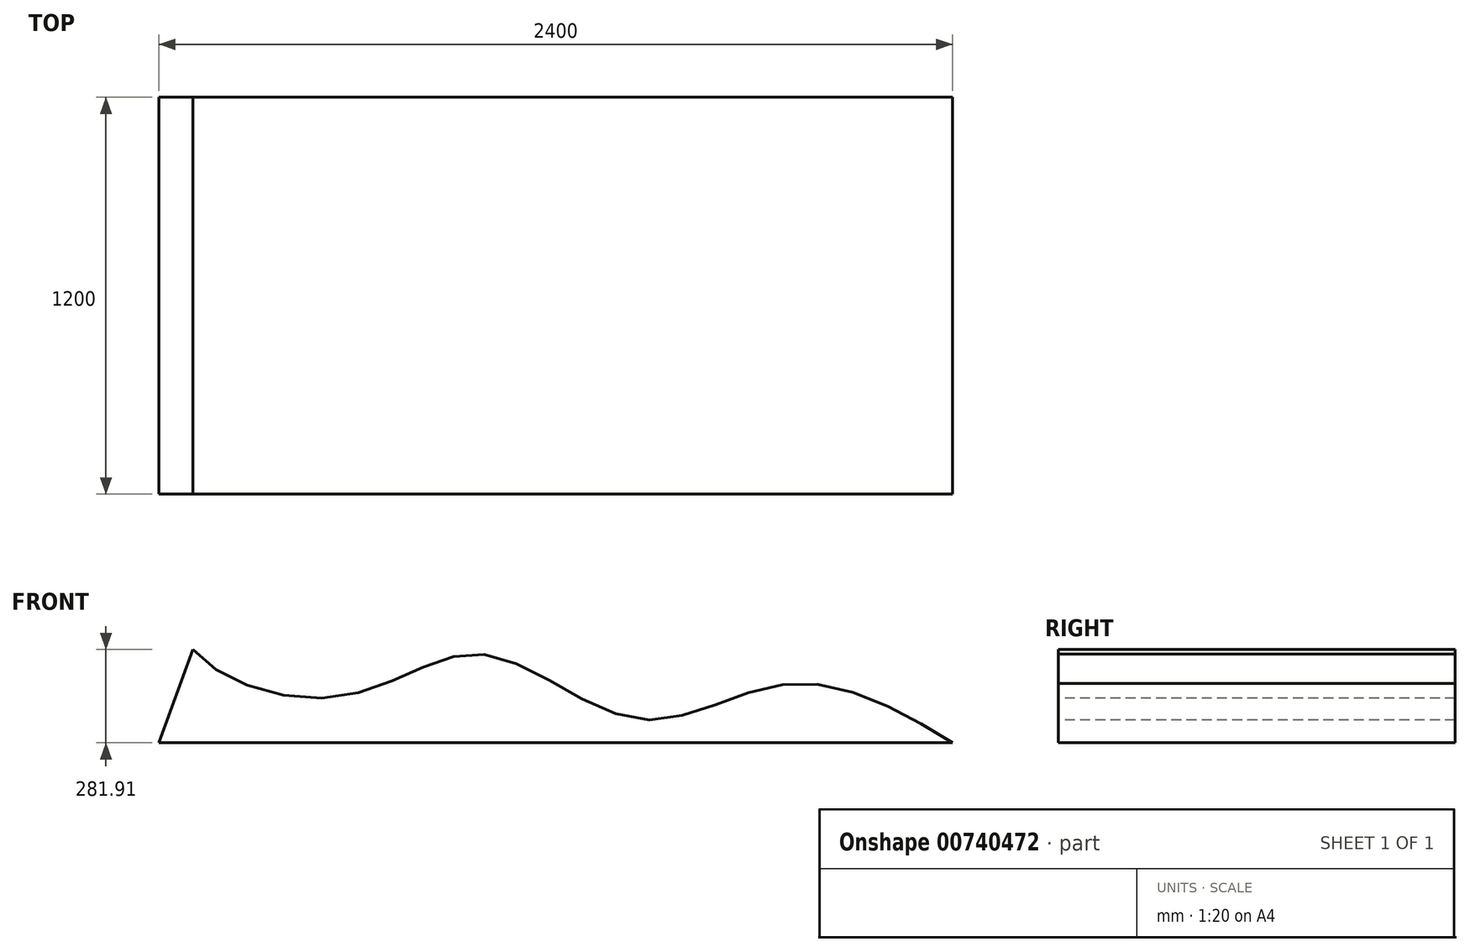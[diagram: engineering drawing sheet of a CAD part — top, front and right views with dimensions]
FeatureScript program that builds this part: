
annotation { "Feature Type Name" : "Feature", "Feature Type Description" : "" }
export const myFeature = defineFeature(function(context is Context, id is Id, definition is map)
    precondition{}
    {
        {
            var Q0;
            Q0=qCreatedBy(makeId("Front.planeOp"),FACE);
            var sketch = newSketch(context, id + "F0", { "sketchPlane" : qUnion([Q0])});
            skLineSegment(sketch, "E0", {"start": v(1167.88, 0) * mm, "end": v(-1232.12, 0) * mm});
            skLineSegment(sketch, "E1", {"start": v(-1232.12, 0) * mm, "end": v(-1129.5, 281.9) * mm});
            skFitSpline(sketch, "E2", {"points": [v(-1129.5, 281.9) * mm, v(-676.87, 141.33) * mm, v(-251.41, 267.57) * mm, v(218.46, 71.2) * mm, v(676.64, 178.74) * mm, v(1167.88, 0) * mm], "startDerivative": vector(1219.48, -1505.13) * mm, "endDerivative": vector(2102.33, -1345.38) * mm});
            skSolve(sketch);
        }
        {
            var Q0;
            Q0=makeQuery(id+"F0.imprint","IMPRINT",FACE,{"disambiguationData":[TD([[makeQuery(id+"F0.imprint","IMPRINT",EDGE,{"derivedFrom":sQuery(id+"F0.wireOp",EDGE,"E0")}),-1.0]])]});
            extrude(context, id + "F1", {"entities" : qUnion([Q0]), "depth" : 1200 * mm, "offsetDistance" : 25 * mm, "symmetric" : true});
        }
    });
